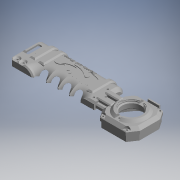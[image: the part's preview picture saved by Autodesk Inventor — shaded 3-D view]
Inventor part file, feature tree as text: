
AUTODESK INVENTOR PART (.ipt)
format: ipt  version: 2018 (Build 220112000, 112)  size: 2,629,632 bytes
history: native  units: mm
features: projected_geometry x7, extrude x5, sketch x5, other x4, chamfer x2
ambient origin geometry x8: Origin, YZ Plane, XZ Plane, XY Plane, X Axis, Y Axis, Z Axis, Center Point
bodies: Body1 (feature_tree)
feature tree (23):
  other  "karikumi.iam"
  other  "conectcover.ipt:1"
  other  "undercover.ipt:1"
  other  "ソリッド1"
  extrude  "押し出し1"  Depth=10.0mm
  chamfer  "面取り1"  Distance=10.0mm
  chamfer  "面取り2"  Distance=1.6mm Angle=45.0deg
  extrude  "押し出し2"  Depth=4.0mm TaperAngle=45.0deg
  extrude  "押し出し3"  Depth=42.7mm
  extrude  "押し出し4"  Depth=2.7mm
  extrude  "押し出し5"  Depth=2.7mm
  sketch  "スケッチ1"
  projected_geometry  "投影ループ1"
  projected_geometry  "投影ループ2"
  sketch  "スケッチ2"
  sketch  "スケッチ3"
  projected_geometry  "投影ループ3"
  sketch  "スケッチ4"
  projected_geometry  "投影ループ4"
  projected_geometry  "投影ループ5"
  sketch  "スケッチ5"
  projected_geometry  "投影ループ6"
  projected_geometry  "投影ループ7"
